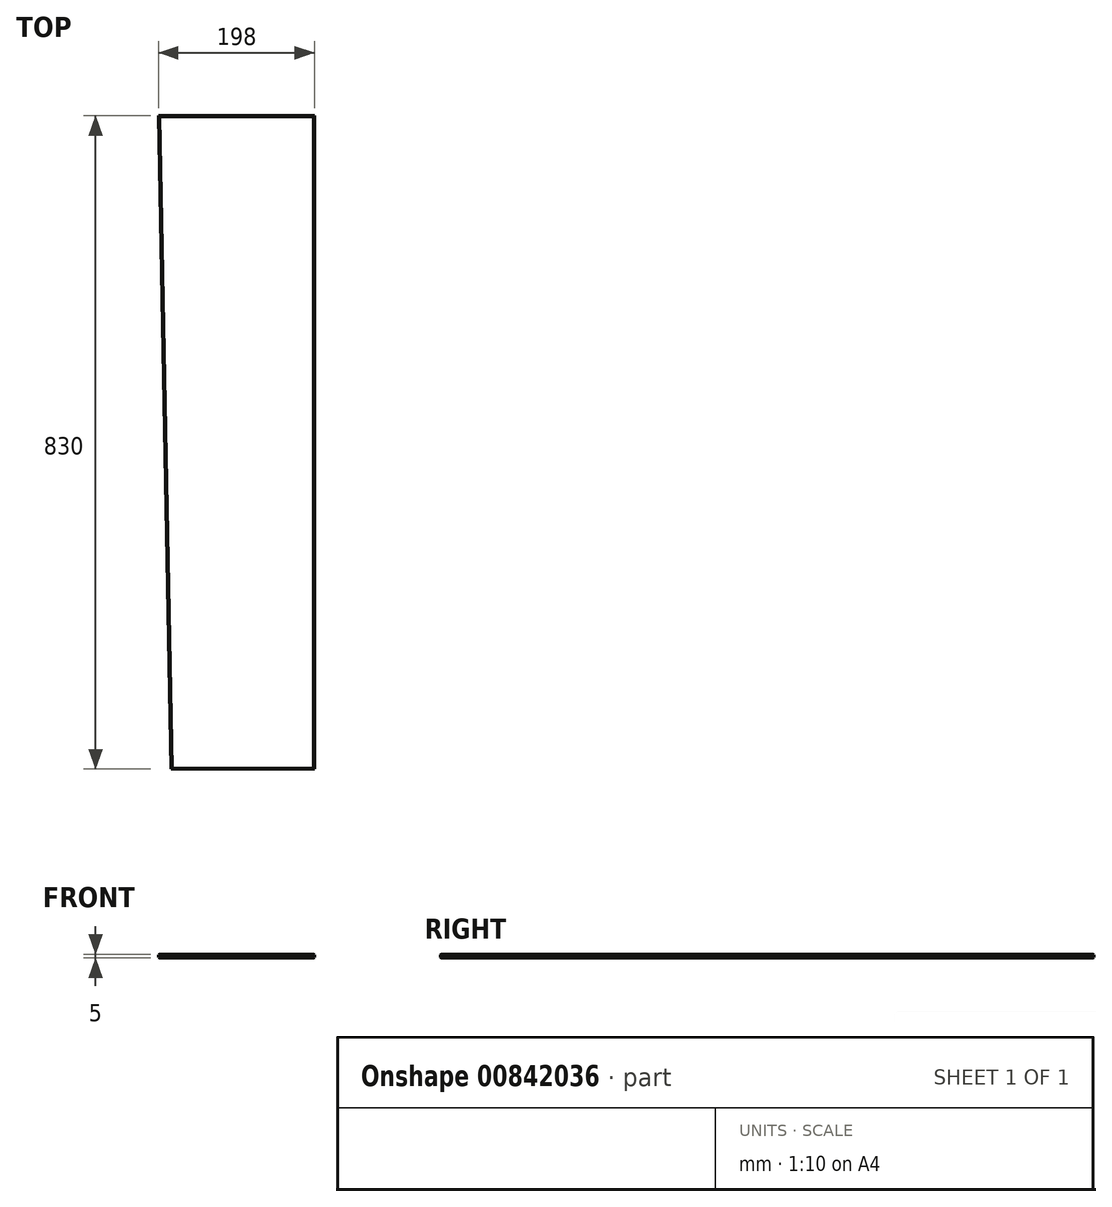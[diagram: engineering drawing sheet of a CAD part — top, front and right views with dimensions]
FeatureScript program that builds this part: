
annotation { "Feature Type Name" : "Feature", "Feature Type Description" : "" }
export const myFeature = defineFeature(function(context is Context, id is Id, definition is map)
    precondition{}
    {
        {
            var Q0;
            Q0=qCreatedBy(makeId("Top.planeOp"),FACE);
            var sketch = newSketch(context, id + "F0", { "sketchPlane" : qUnion([Q0])});
            skLineSegment(sketch, "E0.top", {"start": v(-91, -415) * mm, "end": v(91, -415) * mm});
            skLineSegment(sketch, "E0.right", {"start": v(91, 415) * mm, "end": v(91, -415) * mm});
            skPoint(sketch, "E0.middle", {"position": v(0, 0) * mm});
            skLineSegment(sketch, "E1", {"start": v(91, 415) * mm, "end": v(-107, 415) * mm});
            skLineSegment(sketch, "E2", {"start": v(-107, 415) * mm, "end": v(-91, -415) * mm});
            skSolve(sketch);
        }
        {
            var Q0;
            Q0=makeQuery(id+"F0.imprint","IMPRINT",FACE,{"disambiguationData":[TD([[makeQuery(id+"F0.imprint","IMPRINT",EDGE,{"derivedFrom":sQuery(id+"F0.wireOp",EDGE,"E0.top")}),1.0]])]});
            extrude(context, id + "F1", {"entities" : qUnion([Q0]), "endBound" : BoundingType.SYMMETRIC, "depth" : 5 * mm, "offsetDistance" : 25 * mm});
        }
        {
            var Q0;
            Q0=makeQuery(id+"F1.opExtrude","CAP_EDGE",EDGE,{"disambiguationData":[OSD([sQuery(id+"F0.wireOp",EDGE,"E2")])],"isStart":false});
            var Q1;
            Q1=makeQuery(id+"F1.opExtrude","CAP_EDGE",EDGE,{"disambiguationData":[OSD([sQuery(id+"F0.wireOp",EDGE,"E2")])],"isStart":true});
            var Q2;
            Q2=makeQuery(id+"F1.opExtrude","CAP_EDGE",EDGE,{"disambiguationData":[OSD([sQuery(id+"F0.wireOp",EDGE,"E1")])],"isStart":false});
            var Q3;
            Q3=makeQuery(id+"F1.opExtrude","CAP_EDGE",EDGE,{"disambiguationData":[OSD([sQuery(id+"F0.wireOp",EDGE,"E1")])],"isStart":true});
            var Q4;
            Q4=makeQuery(id+"F1.opExtrude","CAP_EDGE",EDGE,{"disambiguationData":[OSD([sQuery(id+"F0.wireOp",EDGE,"E0.right")])],"isStart":false});
            var Q5;
            Q5=makeQuery(id+"F1.opExtrude","CAP_EDGE",EDGE,{"disambiguationData":[OSD([sQuery(id+"F0.wireOp",EDGE,"E0.right")])],"isStart":true});
            var Q6;
            Q6=makeQuery(id+"F1.opExtrude","CAP_EDGE",EDGE,{"disambiguationData":[OSD([sQuery(id+"F0.wireOp",EDGE,"E0.top")])],"isStart":false});
            var Q7;
            Q7=makeQuery(id+"F1.opExtrude","CAP_EDGE",EDGE,{"disambiguationData":[OSD([sQuery(id+"F0.wireOp",EDGE,"E0.top")])],"isStart":true});
            chamfer(context, id + "F2", {"entities" : qUnion([Q0, Q1, Q2, Q3, Q4, Q5, Q6, Q7]), "width" : 1 * mm, "tangentPropagation" : true});
        }
    });
